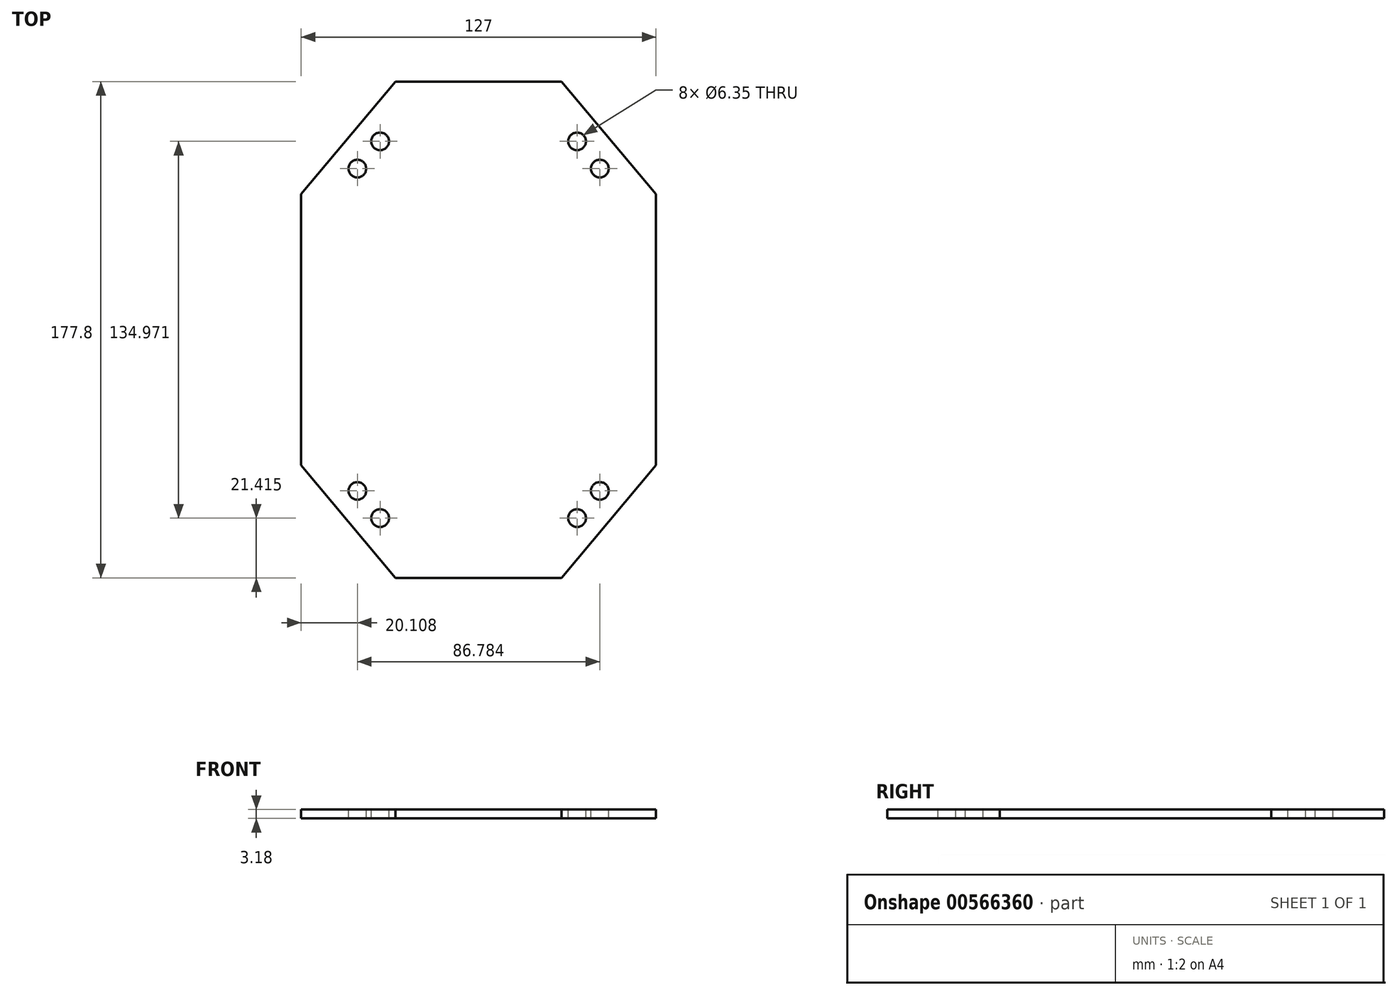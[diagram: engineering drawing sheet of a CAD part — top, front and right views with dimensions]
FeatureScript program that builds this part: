
annotation { "Feature Type Name" : "Feature", "Feature Type Description" : "" }
export const myFeature = defineFeature(function(context is Context, id is Id, definition is map)
    precondition{}
    {
        {
            var Q0;
            Q0=qCreatedBy(makeId("Top.planeOp"),FACE);
            var sketch = newSketch(context, id + "F0", { "sketchPlane" : qUnion([Q0])});
            skLineSegment(sketch, "E0", {"start": v(-29.75, 88.9) * mm, "end": v(29.75, 88.9) * mm});
            skLineSegment(sketch, "E1", {"start": v(29.75, 88.9) * mm, "end": v(63.5, 48.55) * mm});
            skLineSegment(sketch, "E2", {"start": v(63.5, 48.55) * mm, "end": v(63.5, -48.55) * mm});
            skLineSegment(sketch, "E3", {"start": v(63.5, -48.55) * mm, "end": v(29.75, -88.9) * mm});
            skLineSegment(sketch, "E4", {"start": v(29.75, -88.9) * mm, "end": v(-29.75, -88.9) * mm});
            skLineSegment(sketch, "E5", {"start": v(-29.75, -88.9) * mm, "end": v(-63.5, -48.55) * mm});
            skLineSegment(sketch, "E6", {"start": v(-63.5, -48.55) * mm, "end": v(-63.5, 48.55) * mm});
            skLineSegment(sketch, "E7", {"start": v(-63.5, 48.55) * mm, "end": v(-29.75, 88.9) * mm});
            skSolve(sketch);
        }
        {
            var Q0;
            Q0=makeQuery(id+"F0.imprint","IMPRINT",FACE,{"disambiguationData":[TD([[makeQuery(id+"F0.imprint","IMPRINT",EDGE,{"derivedFrom":sQuery(id+"F0.wireOp",EDGE,"E0")}),-1.0]])]});
            extrude(context, id + "F1", {"entities" : qUnion([Q0]), "depth" : 3.17 * mm, "offsetDistance" : 25.4 * mm});
        }
        {
            var Q0;
            Q0=makeQuery(id+"F1.opExtrude","CAP_FACE",FACE,{"disambiguationData":[OSD([sQuery(id+"F0.wireOp",EDGE,"E0"),sQuery(id+"F0.wireOp",EDGE,"E1"),sQuery(id+"F0.wireOp",EDGE,"E2"),sQuery(id+"F0.wireOp",EDGE,"E3"),sQuery(id+"F0.wireOp",EDGE,"E4"),sQuery(id+"F0.wireOp",EDGE,"E5"),sQuery(id+"F0.wireOp",EDGE,"E6"),sQuery(id+"F0.wireOp",EDGE,"E7")])],"isStart":false});
            var sketch = newSketch(context, id + "F2", { "sketchPlane" : qUnion([Q0])});
            skCircle(sketch, "E8", {"center": v(-43.4, 57.74) * mm, "radius": 3.18 * mm});
            skCircle(sketch, "E9", {"center": v(-35.24, 67.49) * mm, "radius": 3.18 * mm});
            skCircle(sketch, "E10", {"center": v(35.24, 67.49) * mm, "radius": 3.18 * mm});
            skCircle(sketch, "E11", {"center": v(43.4, 57.74) * mm, "radius": 3.18 * mm});
            skCircle(sketch, "E12", {"center": v(35.24, -67.49) * mm, "radius": 3.18 * mm});
            skCircle(sketch, "E13", {"center": v(43.4, -57.74) * mm, "radius": 3.18 * mm});
            skCircle(sketch, "E14", {"center": v(-35.24, -67.49) * mm, "radius": 3.18 * mm});
            skCircle(sketch, "E15", {"center": v(-43.4, -57.74) * mm, "radius": 3.18 * mm});
            skSolve(sketch);
        }
        {
            var Q0;
            Q0=makeQuery(id+"F2.imprint","IMPRINT",FACE,{"disambiguationData":[TD([[makeQuery(id+"F2.imprint","IMPRINT",EDGE,{"derivedFrom":sQuery(id+"F2.wireOp",EDGE,"E8")}),1.0]])]});
            var Q1;
            Q1=makeQuery(id+"F2.imprint","IMPRINT",FACE,{"disambiguationData":[TD([[makeQuery(id+"F2.imprint","IMPRINT",EDGE,{"derivedFrom":sQuery(id+"F2.wireOp",EDGE,"E9")}),1.0]])]});
            var Q2;
            Q2=makeQuery(id+"F2.imprint","IMPRINT",FACE,{"disambiguationData":[TD([[makeQuery(id+"F2.imprint","IMPRINT",EDGE,{"derivedFrom":sQuery(id+"F2.wireOp",EDGE,"E10")}),1.0]])]});
            var Q3;
            Q3=makeQuery(id+"F2.imprint","IMPRINT",FACE,{"disambiguationData":[TD([[makeQuery(id+"F2.imprint","IMPRINT",EDGE,{"derivedFrom":sQuery(id+"F2.wireOp",EDGE,"E11")}),1.0]])]});
            var Q4;
            Q4=makeQuery(id+"F2.imprint","IMPRINT",FACE,{"disambiguationData":[TD([[makeQuery(id+"F2.imprint","IMPRINT",EDGE,{"derivedFrom":sQuery(id+"F2.wireOp",EDGE,"E13")}),1.0]])]});
            var Q5;
            Q5=makeQuery(id+"F2.imprint","IMPRINT",FACE,{"disambiguationData":[TD([[makeQuery(id+"F2.imprint","IMPRINT",EDGE,{"derivedFrom":sQuery(id+"F2.wireOp",EDGE,"E12")}),1.0]])]});
            var Q6;
            Q6=makeQuery(id+"F2.imprint","IMPRINT",FACE,{"disambiguationData":[TD([[makeQuery(id+"F2.imprint","IMPRINT",EDGE,{"derivedFrom":sQuery(id+"F2.wireOp",EDGE,"E14")}),1.0]])]});
            var Q7;
            Q7=makeQuery(id+"F2.imprint","IMPRINT",FACE,{"disambiguationData":[TD([[makeQuery(id+"F2.imprint","IMPRINT",EDGE,{"derivedFrom":sQuery(id+"F2.wireOp",EDGE,"E15")}),1.0]])]});
            extrude(context, id + "F3", {"entities" : qUnion([Q0, Q1, Q2, Q3, Q4, Q5, Q6, Q7]), "operationType" : NewBodyOperationType.REMOVE, "oppositeDirection" : true, "depth" : 25.4 * mm, "offsetDistance" : 25.4 * mm});
        }
    });
